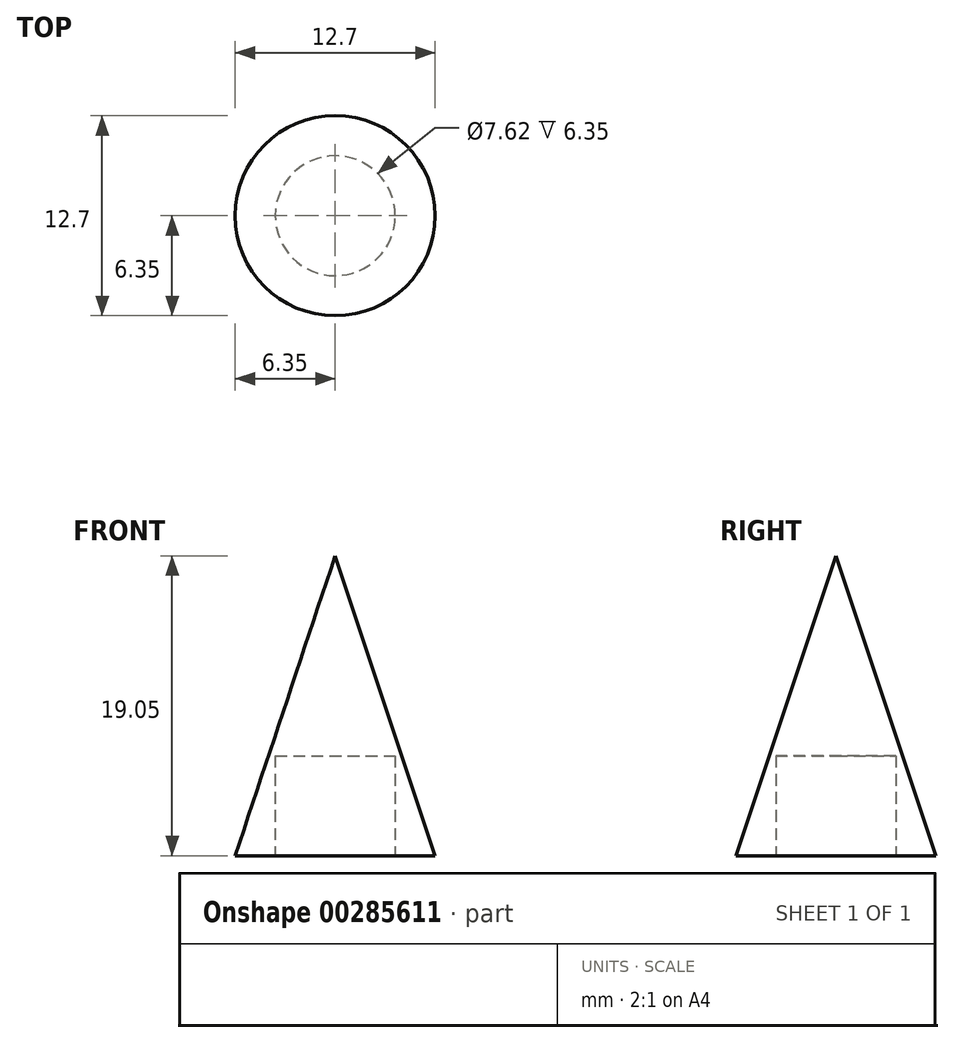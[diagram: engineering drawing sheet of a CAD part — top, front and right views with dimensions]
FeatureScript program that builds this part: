
annotation { "Feature Type Name" : "Feature", "Feature Type Description" : "" }
export const myFeature = defineFeature(function(context is Context, id is Id, definition is map)
    precondition{}
    {
        {
            var Q0;
            Q0=qCreatedBy(makeId("Front.planeOp"),FACE);
            var sketch = newSketch(context, id + "F0", { "sketchPlane" : qUnion([Q0])});
            skLineSegment(sketch, "E0", {"start": v(0, 0) * mm, "end": v(0, 19.05) * mm});
            skLineSegment(sketch, "E1", {"start": v(0, 0) * mm, "end": v(6.35, 0) * mm});
            skLineSegment(sketch, "E2", {"start": v(0, 19.05) * mm, "end": v(6.35, 0) * mm});
            skLineSegment(sketch, "E3", {"start": v(0, 22.5) * mm, "end": v(0, -12.82) * mm, "construction": true});
            skSolve(sketch);
        }
        {
            var Q0;
            Q0 = qSketchRegion(id + "F0", true);
            var Q1;
            Q1=sQuery(id+"F0.wireOp",EDGE,"E3");
            revolve(context, id + "F1", {"entities" : qUnion([Q0]), "axis" : qUnion([Q1]), "revolveType" : RevolveType.FULL});
        }
        {
            var Q0;
            Q0=makeQuery(id+"F1.opRevolve","SWEPT_FACE",FACE,{"disambiguationData":[OSD([sQuery(id+"F0.wireOp",EDGE,"E1")])]});
            var sketch = newSketch(context, id + "F2", { "sketchPlane" : qUnion([Q0])});
            skCircle(sketch, "E4", {"center": v(0, 0) * mm, "radius": 3.81 * mm});
            skSolve(sketch);
        }
        {
            var Q0;
            Q0 = qSketchRegion(id + "F2", true);
            extrude(context, id + "F3", {"entities" : qUnion([Q0]), "operationType" : NewBodyOperationType.REMOVE, "oppositeDirection" : true, "depth" : 6.35 * mm});
        }
    });
